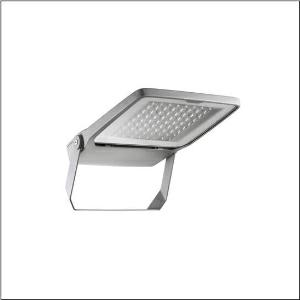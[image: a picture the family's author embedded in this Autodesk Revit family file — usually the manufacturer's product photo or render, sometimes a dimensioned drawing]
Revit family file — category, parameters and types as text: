
# Revit family: floodlight_fl_20_mini___pl61_5xa7672c1c1ac_df0d
name_source: partatom
category: Lighting Fixtures
units: mm (PartAtom-declared; Revit-internal decimal feet)

## family parameters
Cut with Voids When Loaded = No
Host = Face
Light Source = No
Part Type = Normal
Room Calculation Point = No
Round Connector Dimension = Use Diameter
Shared = No

## types (1)
- --- (1 x LED 3000K / CRI = 80 (unbekannt), 9760 lm, 3000K)
    Apparent Load = 96 VA
    CIE Flux Codes = 33 65 98 100 100
    Color Rendering = 80
    Color Temperature = 3000K
    Default Elevation = 1800 mm
    Description = Floodlight FL 20 mini, floodlight, primary light control with lens, of plastic, primary optical cover: protective disc, of toughened safety glass, transparent, light distribution: PL61, light emission: direct distribution, primary light characteristic: asymmetric, installation type: surface-mounted, LED, High Power LED, rated luminous flux: 9.760lm, luminous efficacy: 102lm/W, light colour: 830, colour temperature: 3000K, control gear: ECG Plus, control: flexible luminous flux parameterisation, time-dependent luminous flux control, digital communication interface, power reduction, overheat protection, electronic power reduction, with terminal, 5-pole, max. 2.5mm², mains connection: 220..240V, AC, 50/60Hz, rated input power: 96W, LED unit, of diecast aluminium, powder-coated, Siteco® metallic grey (DB 702S), corrosivity category C5 mid according to DIN EN ISO 12944, incl. 1x M20 cable gland for cable Ø 6.5..12mm, length: 446mm, width: 355mm, height: 62mm, housing frame, of diecast aluminium, powder-coated, Siteco® metallic grey (DB 702S), mounting bracket, of steel, powder-coated, Siteco® metallic grey (DB 702S), DALI, protection rating (complete): IP66, insulation class (complete): insulation class II (safety insulation), certification: CE, ENEC, VDE, protection symbol: D, permissible operating ambient temperature: -40..+40°C, permissible operating ambient temperature for outdoor applications: -40..+50°C, standard: DIN EN 12944, packaging unit: 1 piece

Light Distribution: PL61
    Height = 62 mm  [stored 0.203412 ft]
    Lamp = 1 x LED 3000K / CRI >= 80 (unbekannt)
    Lamp Light Flux = 9760 lm
    Lamp count = 1
    Length = 467 mm
    Luminous efficacy = 102 lm/W
    Manufacturer = Siteco
    ModVariant = No
    Model = 5XA7672C1C1AC
    Mounting Place = Wall
    Mounting Type = Surface mounted
    Number of Poles = 1
    OnlyDefault = Yes
    Power Factor = 1
    Product Name = Floodlight FL 20 mini | PL61
    Product group = floodlight | wall mounted
    ProductGroupID = 2001
    Protection Class = Protection class II
    Protection Degree = IP 66
    RLX_Detail_Level = 1
    RLX_Emergency_Light_Flux = 0 lm
    RLX_Emergency_Type = 0
    RLX_Emergency_Type_DB = No
    RlxData = <blob elided: 74189 chars, md5=c5c57c21>
    Socket = socket
    Standby Power = 0 W
    System Light Flux = 9760 lm
    System Power = 96 W
    Type Comments = factory setting: luminous flux: 100 % | dim-lin: 254 | 500 mA
    Type Image = l_1005948.jpg
    URL = http://relux.com
    VarID = @adj_163485
    Voltage = 0 V
    Weight = 0.00 kg
    Width = 335 mm

note: [stored X ft] marks values corroborated as IEEE doubles in the binary element streams (Revit-internal decimal feet)

## geometry (parser evidence)
native form markers: Blend x4, Sweep x13
no freeform markers — native parametric forms only
